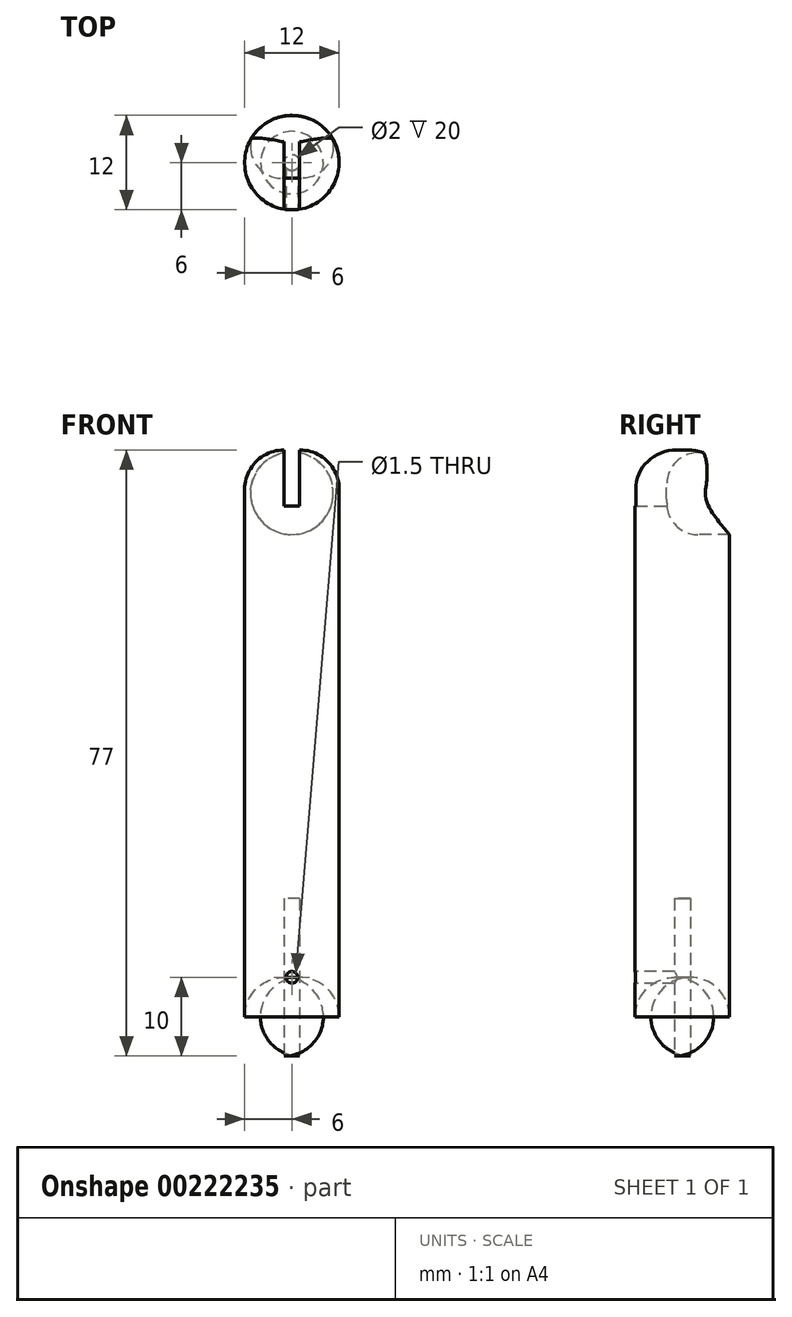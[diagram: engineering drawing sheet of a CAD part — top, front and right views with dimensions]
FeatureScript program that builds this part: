
annotation { "Feature Type Name" : "Feature", "Feature Type Description" : "" }
export const myFeature = defineFeature(function(context is Context, id is Id, definition is map)
    precondition{}
    {
        {
            var Q0;
            Q0=qCreatedBy(makeId("Top.planeOp"),FACE);
            var sketch = newSketch(context, id + "F0", { "sketchPlane" : qUnion([Q0])});
            skCircle(sketch, "E0", {"center": v(0, 0) * mm, "radius": 6 * mm});
            skCircle(sketch, "E1", {"center": v(0, 0) * mm, "radius": 1 * mm});
            skSolve(sketch);
        }
        {
            var Q0;
            Q0=makeQuery(id+"F0.imprint","IMPRINT",FACE,{"disambiguationData":[TD([[makeQuery(id+"F0.imprint","IMPRINT",EDGE,{"derivedFrom":sQuery(id+"F0.wireOp",EDGE,"E0")}),1.0]])]});
            var Q1;
            Q1=makeQuery(id+"F0.imprint","IMPRINT",FACE,{"disambiguationData":[TD([[makeQuery(id+"F0.imprint","IMPRINT",EDGE,{"derivedFrom":sQuery(id+"F0.wireOp",EDGE,"E1")}),1.0]])]});
            extrude(context, id + "F1", {"entities" : qUnion([Q0, Q1]), "depth" : 77 * mm, "offsetDistance" : 25 * mm});
        }
        {
            var Q0;
            Q0=makeQuery(id+"F1.opExtrude","CAP_EDGE",EDGE,{"disambiguationData":[OSD([sQuery(id+"F0.wireOp",EDGE,"E0")])],"isStart":true});
            fillet(context, id + "F2", {"entities" : qUnion([Q0]), "radius" : 5 * mm, "tangentPropagation" : true, "allowEdgeOverflow" : false});
        }
        {
            var Q0;
            Q0=qCreatedBy(makeId("Front.planeOp"),FACE);
            var sketch = newSketch(context, id + "F3", { "sketchPlane" : qUnion([Q0])});
            skPoint(sketch, "E2", {"position": v(0, 71.5) * mm});
            skCircle(sketch, "E3", {"center": v(0, 71.5) * mm, "radius": 5.25 * mm});
            skPoint(sketch, "E4", {"position": v(0, 76.75) * mm});
            skPoint(sketch, "E5", {"position": v(0, 5.5) * mm});
            skSolve(sketch);
        }
        {
            var Q0;
            Q0 = qSketchRegion(id + "F3", true);
            extrude(context, id + "F4", {"entities" : qUnion([Q0]), "operationType" : NewBodyOperationType.REMOVE, "oppositeDirection" : true, "depth" : 8.5 * mm, "offsetDistance" : 25 * mm, "hasSecondDirection" : true, "secondDirectionOppositeDirection" : false, "secondDirectionDepth" : 2 * mm});
        }
        {
            var Q0;
            Q0=makeQuery(id+"F1.opExtrude","CAP_EDGE",EDGE,{"disambiguationData":[OSD([sQuery(id+"F0.wireOp",EDGE,"E0")])],"isStart":false});
            fillet(context, id + "F5", {"entities" : qUnion([Q0]), "radius" : 5 * mm, "tangentPropagation" : true, "allowEdgeOverflow" : false});
        }
        {
            var Q0;
            Q0=qCreatedBy(makeId("Front.planeOp"),FACE);
            var sketch = newSketch(context, id + "F6", { "sketchPlane" : qUnion([Q0])});
            skPoint(sketch, "E6", {"position": v(0, 76.87) * mm});
            skLineSegment(sketch, "E7.bottom", {"start": v(1, 83.87) * mm, "end": v(-1, 83.87) * mm});
            skLineSegment(sketch, "E7.top", {"start": v(1, 69.87) * mm, "end": v(-1, 69.87) * mm});
            skLineSegment(sketch, "E7.left", {"start": v(1, 83.87) * mm, "end": v(1, 69.87) * mm});
            skLineSegment(sketch, "E7.right", {"start": v(-1, 83.87) * mm, "end": v(-1, 69.87) * mm});
            skSolve(sketch);
        }
        {
            var Q0;
            Q0 = qSketchRegion(id + "F6", true);
            extrude(context, id + "F7", {"entities" : qUnion([Q0]), "operationType" : NewBodyOperationType.REMOVE, "depth" : 25 * mm, "offsetDistance" : 25 * mm, "symmetric" : true});
        }
        {
            var Q0;
            Q0=makeQuery(id+"F4.boolean.opBoolean","COPY",EDGE,{"derivedFrom":makeQuery(id+"F4.opExtrude","CAP_EDGE",EDGE,{"disambiguationData":[OSD([sQuery(id+"F3.wireOp",EDGE,"E3")])],"isStart":true})});
            fillet(context, id + "F8", {"entities" : qUnion([Q0]), "radius" : 4 * mm, "tangentPropagation" : true, "allowEdgeOverflow" : false});
        }
        {
            var Q0;
            Q0=makeQuery(id+"F0.imprint","IMPRINT",FACE,{"disambiguationData":[TD([[makeQuery(id+"F0.imprint","IMPRINT",EDGE,{"derivedFrom":sQuery(id+"F0.wireOp",EDGE,"E1")}),1.0]])]});
            extrude(context, id + "F9", {"entities" : qUnion([Q0]), "operationType" : NewBodyOperationType.REMOVE, "depth" : 20 * mm, "offsetDistance" : 25 * mm});
        }
        {
            var Q0;
            Q0=qCreatedBy(makeId("Front.planeOp"),FACE);
            var sketch = newSketch(context, id + "F10", { "sketchPlane" : qUnion([Q0])});
            skPoint(sketch, "E8", {"position": v(0, 10) * mm});
            skSolve(sketch);
        }
        {
            var Q0;
            Q0=sQuery(id+"F10.wireOp",VERTEX,"E8");
            var Q1;
            Q1=makeQuery(id+"F1.opExtrude","SWEPT_BODY",BODY,{"disambiguationData":[OSD([sQuery(id+"F0.wireOp",EDGE,"E0")])]});
            hole(context, id + "F11", {"style" : HoleStyle.SIMPLE, "endStyle" : HoleEndStyle.BLIND, "oppositeDirection" : true, "holeDiameter" : 1.5 * mm, "majorDiameter" : 5 * mm, "holeDepth" : 7 * mm, "isTappedThrough" : true, "tappedDepth" : 12 * mm, "tapClearance" : 3, "locations" : qUnion([Q0]), "scope" : qUnion([Q1])});
        }
    });
